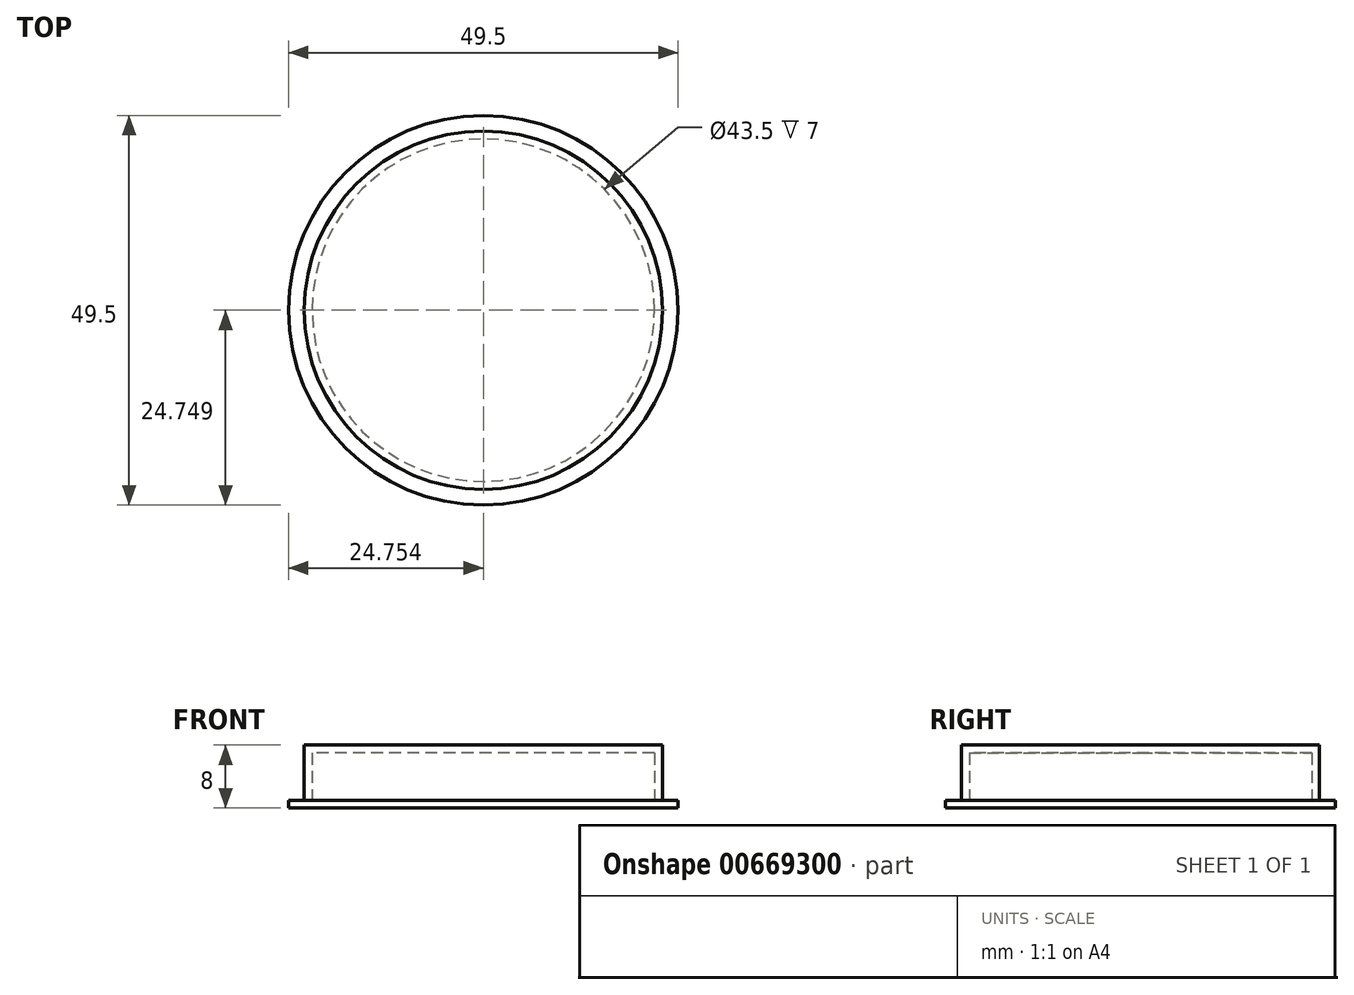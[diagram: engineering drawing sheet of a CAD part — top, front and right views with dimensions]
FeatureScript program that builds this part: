
annotation { "Feature Type Name" : "Feature", "Feature Type Description" : "" }
export const myFeature = defineFeature(function(context is Context, id is Id, definition is map)
    precondition{}
    {
        {
            var Q0;
            Q0=qCreatedBy(makeId("Top.planeOp"),FACE);
            var sketch = newSketch(context, id + "F0", { "sketchPlane" : qUnion([Q0])});
            skCircle(sketch, "E0", {"center": v(-30, 13.64) * mm, "radius": 21.75 * mm});
            skCircle(sketch, "E1", {"center": v(-30, 13.64) * mm, "radius": 20.75 * mm});
            skCircle(sketch, "E2", {"center": v(-30, 13.64) * mm, "radius": 24.75 * mm});
            skCircle(sketch, "E3", {"center": v(-30, 13.64) * mm, "radius": 22.75 * mm});
            skSolve(sketch);
        }
        {
            var Q0;
            Q0=makeQuery(id+"F0.imprint","IMPRINT",FACE,{"disambiguationData":[TD([[makeQuery(id+"F0.imprint","IMPRINT",EDGE,{"derivedFrom":sQuery(id+"F0.wireOp",EDGE,"E2")}),1.0]])]});
            extrude(context, id + "F1", {"entities" : qUnion([Q0]), "depth" : 1 * mm, "offsetDistance" : 25 * mm});
        }
        {
            var Q0;
            Q0=makeQuery(id+"F0.imprint","IMPRINT",FACE,{"disambiguationData":[TD([[makeQuery(id+"F0.imprint","IMPRINT",EDGE,{"derivedFrom":sQuery(id+"F0.wireOp",EDGE,"E1")}),1.0]])]});
            var Q1;
            Q1=makeQuery(id+"F0.imprint","IMPRINT",FACE,{"disambiguationData":[TD([[makeQuery(id+"F0.imprint","IMPRINT",EDGE,{"derivedFrom":sQuery(id+"F0.wireOp",EDGE,"E0")}),-1.0]])]});
            var Q2;
            Q2=makeQuery(id+"F0.imprint","IMPRINT",FACE,{"disambiguationData":[TD([[makeQuery(id+"F0.imprint","IMPRINT",EDGE,{"derivedFrom":sQuery(id+"F0.wireOp",EDGE,"E0")}),1.0]])]});
            extrude(context, id + "F2", {"entities" : qUnion([Q0, Q1, Q2]), "operationType" : NewBodyOperationType.ADD, "depth" : 8 * mm, "offsetDistance" : 25 * mm});
        }
        {
            var Q0;
            {var subQ0=sQuery(id+"F0.wireOp",EDGE,"E3");Q0=makeQuery(id+"F2.boolean.opBoolean","MERGE",FACE,{"derivedFrom":[makeQuery(id+"F1.opExtrude","CAP_FACE",FACE,{"disambiguationData":[OSD([sQuery(id+"F0.wireOp",EDGE,"E2"),subQ0])],"isStart":true}),makeQuery(id+"F2.opExtrude","CAP_FACE",FACE,{"disambiguationData":[OSD([subQ0])],"isStart":true})]});}
            shell(context, id + "F3", {"entities" : qUnion([Q0]), "thickness" : 1 * mm});
        }
    });
